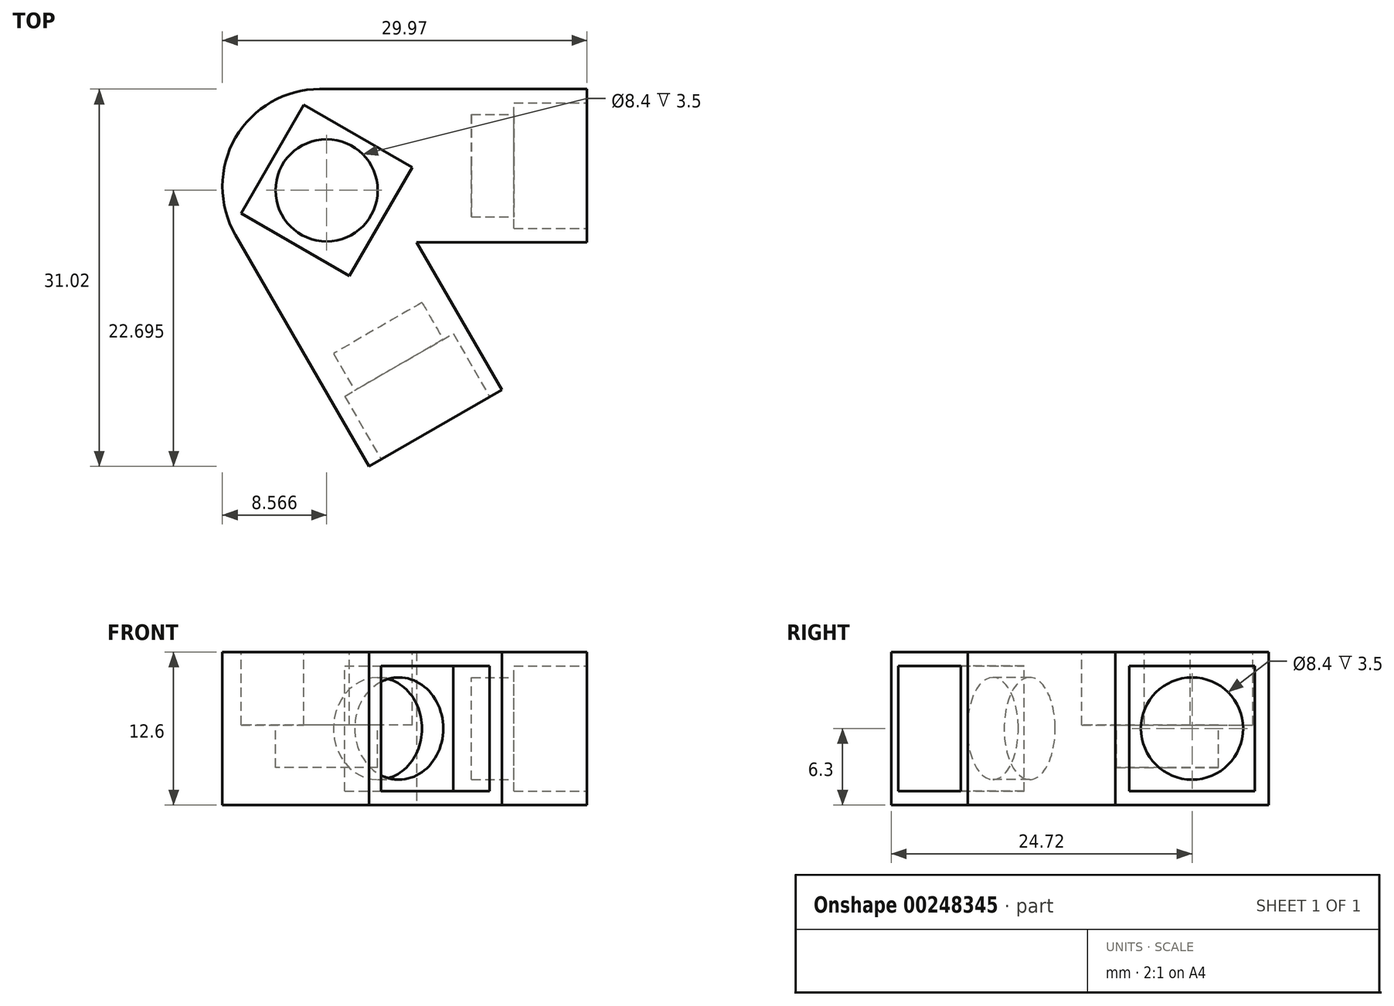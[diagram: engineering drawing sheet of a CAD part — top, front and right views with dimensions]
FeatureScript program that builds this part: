
annotation { "Feature Type Name" : "Feature", "Feature Type Description" : "" }
export const myFeature = defineFeature(function(context is Context, id is Id, definition is map)
    precondition{}
    {
        {
            var Q0;
            Q0=qCreatedBy(makeId("Top.planeOp"),FACE);
            var sketch = newSketch(context, id + "F0", { "sketchPlane" : qUnion([Q0])});
            skLineSegment(sketch, "E0", {"start": v(0, 0) * mm, "end": v(-21.97, 0) * mm});
            skLineSegment(sketch, "E1", {"start": v(-28.9, -12) * mm, "end": v(-17.91, -31.02) * mm});
            skLineSegment(sketch, "E2", {"start": v(-17.91, -31.02) * mm, "end": v(-7, -24.72) * mm});
            skLineSegment(sketch, "E3", {"start": v(-7, -24.72) * mm, "end": v(-14, -12.6) * mm});
            skLineSegment(sketch, "E4", {"start": v(-14, -12.6) * mm, "end": v(0, -12.6) * mm});
            skLineSegment(sketch, "E5", {"start": v(0, -12.6) * mm, "end": v(0, 0) * mm});
            skPoint(sketch, "E6.visualSharp", {"position": v(-35.82, 0) * mm});
            skArc(sketch, "E6.filletArc", {"start": v(-21.97, 0) * mm, "mid": v(-28.9, -4) * mm, "end": v(-28.9, -12) * mm});
            skSolve(sketch);
        }
        {
            var Q0;
            Q0 = qSketchRegion(id + "F0", true);
            extrude(context, id + "F1", {"entities" : qUnion([Q0]), "depth" : 12.6 * mm});
        }
        {
            var Q0;
            Q0=makeQuery(id+"F1.opExtrude","SWEPT_FACE",FACE,{"disambiguationData":[OSD([sQuery(id+"F0.wireOp",EDGE,"E2")])]});
            var sketch = newSketch(context, id + "F2", { "sketchPlane" : qUnion([Q0])});
            skLineSegment(sketch, "E7.bottom", {"start": v(-29.87, 1.15) * mm, "end": v(-19.57, 1.15) * mm});
            skLineSegment(sketch, "E7.top", {"start": v(-29.87, 11.45) * mm, "end": v(-19.57, 11.45) * mm});
            skLineSegment(sketch, "E7.left", {"start": v(-29.87, 1.15) * mm, "end": v(-29.87, 11.45) * mm});
            skLineSegment(sketch, "E7.right", {"start": v(-19.57, 1.15) * mm, "end": v(-19.57, 11.45) * mm});
            skPoint(sketch, "E7.middle", {"position": v(-24.72, 6.3) * mm});
            skPoint(sketch, "E7.middle.positionSnap0", {"position": v(-18.42, 6.3) * mm});
            skPoint(sketch, "E7.middle.positionSnap1", {"position": v(-24.72, 12.6) * mm});
            skPoint(sketch, "E7.centerSnap0", {"position": v(-18.42, 6.3) * mm});
            skPoint(sketch, "E7.centerSnap1", {"position": v(-24.72, 12.6) * mm});
            skSolve(sketch);
        }
        {
            var Q0;
            Q0 = qSketchRegion(id + "F2", true);
            extrude(context, id + "F3", {"entities" : qUnion([Q0]), "operationType" : NewBodyOperationType.REMOVE, "oppositeDirection" : true, "depth" : 6 * mm});
        }
        {
            var Q0;
            Q0=makeQuery(id+"F1.opExtrude","SWEPT_FACE",FACE,{"disambiguationData":[OSD([sQuery(id+"F0.wireOp",EDGE,"E5")])]});
            var sketch = newSketch(context, id + "F4", { "sketchPlane" : qUnion([Q0])});
            skLineSegment(sketch, "E8.bottom", {"start": v(-11.45, 1.15) * mm, "end": v(-1.15, 1.15) * mm});
            skLineSegment(sketch, "E8.top", {"start": v(-11.45, 11.45) * mm, "end": v(-1.15, 11.45) * mm});
            skLineSegment(sketch, "E8.left", {"start": v(-11.45, 1.15) * mm, "end": v(-11.45, 11.45) * mm});
            skLineSegment(sketch, "E8.right", {"start": v(-1.15, 1.15) * mm, "end": v(-1.15, 11.45) * mm});
            skPoint(sketch, "E8.middle", {"position": v(-6.3, 6.3) * mm});
            skPoint(sketch, "E8.middle.positionSnap0", {"position": v(0, 6.3) * mm});
            skPoint(sketch, "E8.middle.positionSnap1", {"position": v(-6.3, 12.6) * mm});
            skPoint(sketch, "E8.centerSnap0", {"position": v(0, 6.3) * mm});
            skPoint(sketch, "E8.centerSnap1", {"position": v(-6.3, 12.6) * mm});
            skSolve(sketch);
        }
        {
            var Q0;
            Q0 = qSketchRegion(id + "F4", true);
            extrude(context, id + "F5", {"entities" : qUnion([Q0]), "operationType" : NewBodyOperationType.REMOVE, "oppositeDirection" : true, "depth" : 6 * mm});
        }
        {
            var Q0;
            Q0=makeQuery(id+"F5.boolean.opBoolean","COPY",FACE,{"derivedFrom":makeQuery(id+"F5.opExtrude","CAP_FACE",FACE,{"disambiguationData":[OSD([sQuery(id+"F4.wireOp",EDGE,"E8.bottom"),sQuery(id+"F4.wireOp",EDGE,"E8.top"),sQuery(id+"F4.wireOp",EDGE,"E8.left"),sQuery(id+"F4.wireOp",EDGE,"E8.right")])],"isStart":false})});
            var sketch = newSketch(context, id + "F6", { "sketchPlane" : qUnion([Q0])});
            skCircle(sketch, "E9", {"center": v(-6.3, 6.3) * mm, "radius": 4.2 * mm});
            skPoint(sketch, "E9.centerSnap0", {"position": v(-6.3, 11.45) * mm});
            skPoint(sketch, "E9.centerSnap1", {"position": v(-1.15, 6.3) * mm});
            skSolve(sketch);
        }
        {
            var Q0;
            Q0 = qSketchRegion(id + "F6", true);
            extrude(context, id + "F7", {"entities" : qUnion([Q0]), "operationType" : NewBodyOperationType.REMOVE, "oppositeDirection" : true, "depth" : 3.5 * mm});
        }
        {
            var Q0;
            Q0=makeQuery(id+"F3.boolean.opBoolean","COPY",FACE,{"derivedFrom":makeQuery(id+"F3.opExtrude","CAP_FACE",FACE,{"disambiguationData":[OSD([sQuery(id+"F2.wireOp",EDGE,"E7.bottom"),sQuery(id+"F2.wireOp",EDGE,"E7.top"),sQuery(id+"F2.wireOp",EDGE,"E7.left"),sQuery(id+"F2.wireOp",EDGE,"E7.right")])],"isStart":false})});
            var sketch = newSketch(context, id + "F8", { "sketchPlane" : qUnion([Q0])});
            skCircle(sketch, "E10", {"center": v(-24.72, 6.3) * mm, "radius": 4.2 * mm});
            skPoint(sketch, "E10.centerSnap0", {"position": v(-24.72, 11.45) * mm});
            skPoint(sketch, "E10.centerSnap1", {"position": v(-19.57, 6.3) * mm});
            skSolve(sketch);
        }
        {
            var Q0;
            Q0 = qSketchRegion(id + "F8", true);
            extrude(context, id + "F9", {"entities" : qUnion([Q0]), "operationType" : NewBodyOperationType.REMOVE, "oppositeDirection" : true, "depth" : 3.5 * mm});
        }
        {
            var Q0;
            Q0=makeQuery(id+"F1.opExtrude","CAP_FACE",FACE,{"disambiguationData":[OSD([sQuery(id+"F0.wireOp",EDGE,"E0"),sQuery(id+"F0.wireOp",EDGE,"E1"),sQuery(id+"F0.wireOp",EDGE,"E2"),sQuery(id+"F0.wireOp",EDGE,"E3"),sQuery(id+"F0.wireOp",EDGE,"E4"),sQuery(id+"F0.wireOp",EDGE,"E5"),sQuery(id+"F0.wireOp",EDGE,"E6.filletArc")])],"isStart":false});
            var sketch = newSketch(context, id + "F10", { "sketchPlane" : qUnion([Q0])});
            skLineSegment(sketch, "E11", {"start": v(0, 0) * mm, "end": v(-17.91, -31.02) * mm});
            skLineSegment(sketch, "E12", {"start": v(-14.37, -6.44) * mm, "end": v(-19.52, -15.36) * mm});
            skLineSegment(sketch, "E13", {"start": v(-19.52, -15.36) * mm, "end": v(-28.44, -10.21) * mm});
            skLineSegment(sketch, "E14", {"start": v(-28.44, -10.21) * mm, "end": v(-23.29, -1.29) * mm});
            skLineSegment(sketch, "E15", {"start": v(-14.37, -6.44) * mm, "end": v(-23.29, -1.29) * mm});
            skPoint(sketch, "E16.orphan", {"position": v(-16.8, -5.04) * mm});
            skPoint(sketch, "E17.orphan", {"position": v(-25.45, -5.04) * mm});
            skLineSegment(sketch, "E18", {"start": v(-25.86, -5.75) * mm, "end": v(-17.74, -10.44) * mm});
            skSolve(sketch);
        }
        {
            var Q0;
            Q0 = qSketchRegion(id + "F10", true);
            extrude(context, id + "F11", {"entities" : qUnion([Q0]), "operationType" : NewBodyOperationType.REMOVE, "oppositeDirection" : true, "depth" : 6 * mm});
        }
        {
            var Q0;
            Q0=makeQuery(id+"F11.boolean.opBoolean","COPY",FACE,{"derivedFrom":makeQuery(id+"F11.opExtrude","CAP_FACE",FACE,{"disambiguationData":[OSD([sQuery(id+"F10.wireOp",EDGE,"E12"),sQuery(id+"F10.wireOp",EDGE,"E13"),sQuery(id+"F10.wireOp",EDGE,"E14"),sQuery(id+"F10.wireOp",EDGE,"E15")])],"isStart":false})});
            var sketch = newSketch(context, id + "F12", { "sketchPlane" : qUnion([Q0])});
            skLineSegment(sketch, "E19", {"start": v(-18.83, -3.86) * mm, "end": v(-23.98, -12.79) * mm});
            skLineSegment(sketch, "E20", {"start": v(-23.98, -12.79) * mm, "end": v(-21.4, -8.33) * mm});
            skCircle(sketch, "E21", {"center": v(-21.4, -8.33) * mm, "radius": 4.2 * mm});
            skSolve(sketch);
        }
        {
            var Q0;
            Q0 = qSketchRegion(id + "F12", true);
            extrude(context, id + "F13", {"entities" : qUnion([Q0]), "operationType" : NewBodyOperationType.REMOVE, "oppositeDirection" : true, "depth" : 3.5 * mm});
        }
    });
